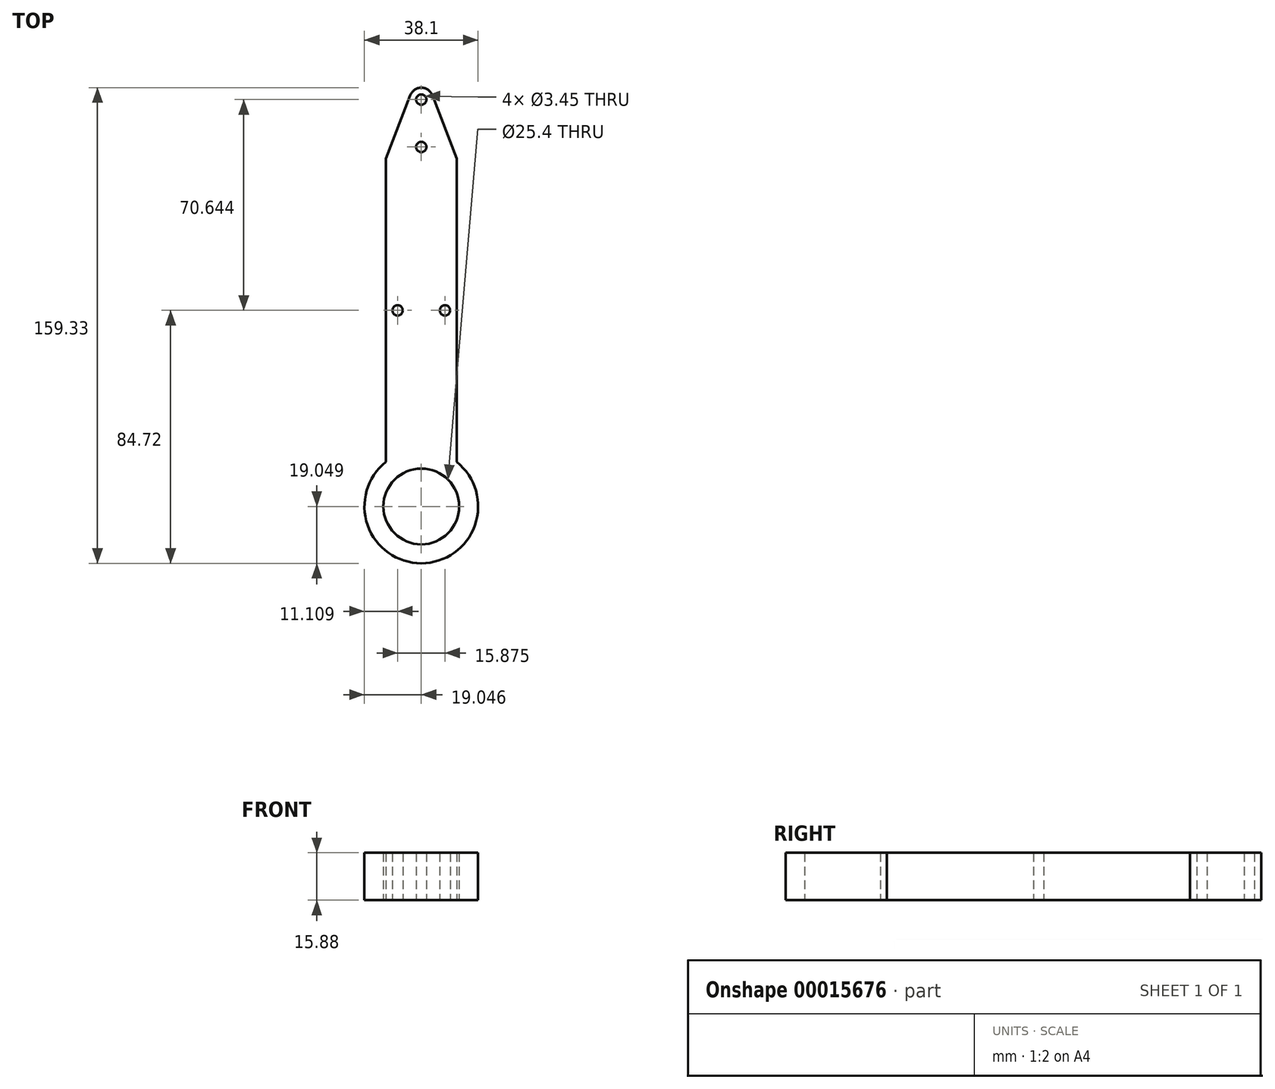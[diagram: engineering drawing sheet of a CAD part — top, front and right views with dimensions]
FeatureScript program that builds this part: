
annotation { "Feature Type Name" : "Feature", "Feature Type Description" : "" }
export const myFeature = defineFeature(function(context is Context, id is Id, definition is map)
    precondition{}
    {
        {
            var Q0;
            Q0=qCreatedBy(makeId("Top.planeOp"),FACE);
            var sketch = newSketch(context, id + "F0", { "sketchPlane" : qUnion([Q0])});
            skLineSegment(sketch, "E0.bottom", {"start": v(0, 0) * mm, "end": v(23.81, 0) * mm, "construction": true});
            skLineSegment(sketch, "E0.top", {"start": v(0, -101.6) * mm, "end": v(23.81, -101.6) * mm, "construction": true});
            skLineSegment(sketch, "E0.left", {"start": v(0, 0) * mm, "end": v(0, -101.6) * mm});
            skLineSegment(sketch, "E0.right", {"start": v(23.81, 0) * mm, "end": v(23.81, -101.6) * mm});
            skLineSegment(sketch, "E1", {"start": v(0, -50.8) * mm, "end": v(3.97, -50.8) * mm});
            skLineSegment(sketch, "E2", {"start": v(3.97, -50.8) * mm, "end": v(11.9, -50.8) * mm});
            skLineSegment(sketch, "E3", {"start": v(11.9, -50.8) * mm, "end": v(19.84, -50.8) * mm, "construction": true});
            skLineSegment(sketch, "E4", {"start": v(19.84, -50.8) * mm, "end": v(23.81, -50.8) * mm, "construction": true});
            skCircle(sketch, "E5", {"center": v(3.97, -50.8) * mm, "radius": 1.73 * mm});
            skCircle(sketch, "E6", {"center": v(19.84, -50.8) * mm, "radius": 1.73 * mm});
            skLineSegment(sketch, "E7", {"start": v(11.9, 0) * mm, "end": v(11.9, 3.97) * mm, "construction": true});
            skLineSegment(sketch, "E8", {"start": v(11.9, 3.97) * mm, "end": v(11.9, 11.9) * mm, "construction": true});
            skLineSegment(sketch, "E9", {"start": v(11.9, 11.9) * mm, "end": v(11.9, 19.84) * mm, "construction": true});
            skLineSegment(sketch, "E10", {"start": v(11.9, 19.84) * mm, "end": v(11.9, 23.81) * mm, "construction": true});
            skArc(sketch, "E11", {"start": v(15.6, 21.27) * mm, "mid": v(11.9, 23.81) * mm, "end": v(8.2, 21.27) * mm});
            skLineSegment(sketch, "E12", {"start": v(0, 0) * mm, "end": v(8.2, 21.27) * mm});
            skLineSegment(sketch, "E13", {"start": v(15.6, 21.27) * mm, "end": v(23.81, 0) * mm});
            skCircle(sketch, "E14", {"center": v(11.9, 19.84) * mm, "radius": 1.73 * mm});
            skCircle(sketch, "E15", {"center": v(11.9, 3.97) * mm, "radius": 1.73 * mm});
            skArc(sketch, "E16", {"start": v(0, -101.6) * mm, "mid": v(11.9, -135.52) * mm, "end": v(23.81, -101.6) * mm});
            skCircle(sketch, "E17", {"center": v(11.9, -116.47) * mm, "radius": 12.7 * mm});
            skSolve(sketch);
        }
        {
            var Q0;
            Q0=qSketchRegion(id+"F0",true);
            extrude(context, id + "F1", {"entities" : qUnion([Q0]), "depth" : 15.88 * mm});
        }
    });
